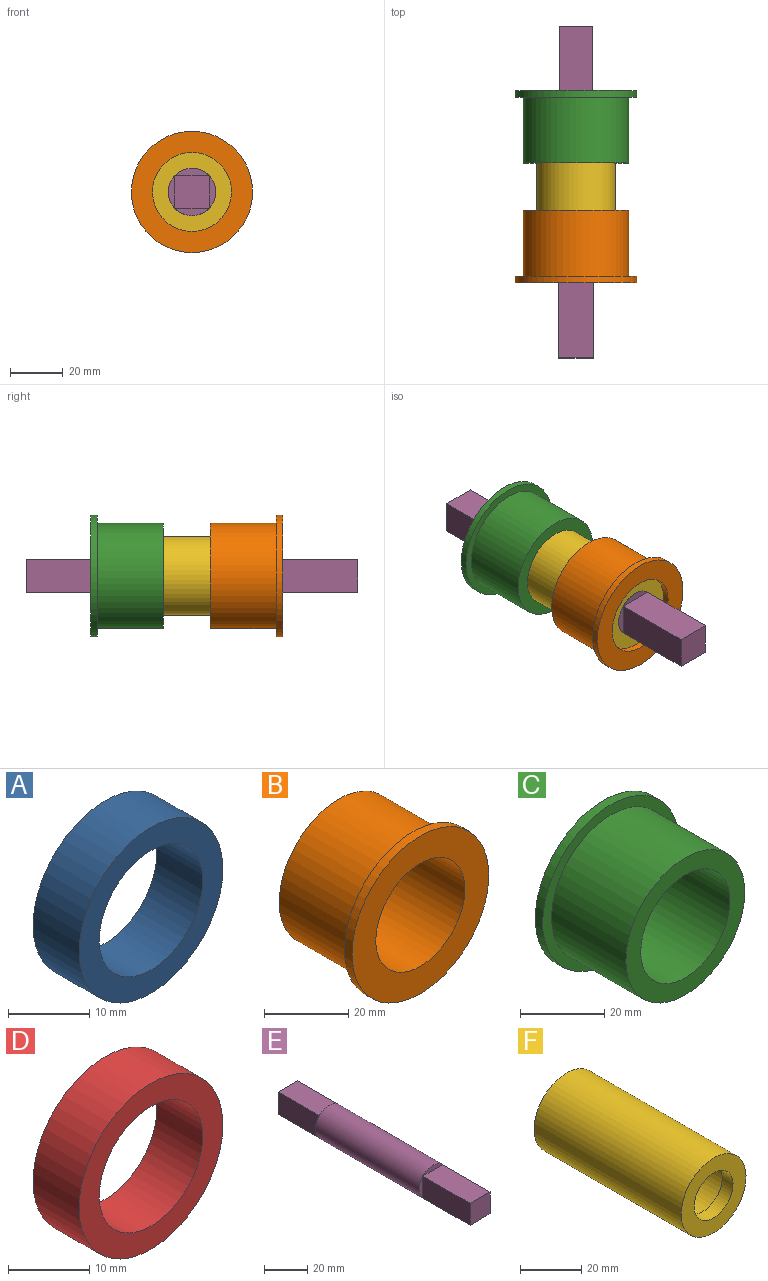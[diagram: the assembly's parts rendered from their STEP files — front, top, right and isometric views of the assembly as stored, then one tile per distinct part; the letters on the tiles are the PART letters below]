
ASSEMBLY  parts=6 mates=10
PART A: 4 faces, bbox 25x8x25 mm
  f0: cylinder r=9mm len=18mm, axis (0,1,0), area 452.4mm2, adj f2,f3
  f1: cylinder r=12.5mm len=25mm, axis (0,1,0), area 628.3mm2, adj f2,f3
  f2: plane 25x25mm, normal (0,-1,0), area 236.4mm2, adj f0,f1
  f3: plane 25x25mm, normal (0,1,0), area 236.4mm2, adj f0,f1
PART B: 6 faces, bbox 46x27.5x46 mm
  f0: cylinder r=15mm len=30mm, axis (0,1,0), area 2591.8mm2, adj f2,f5
  f1: cylinder r=23mm len=46mm, axis (0,1,0), area 361.3mm2, adj f2,f3
  f2: plane 46x46mm, normal (0,-1,0), area 955mm2, adj f0,f1
  f3: plane 46x46mm, normal (0,1,0), area 405.3mm2, adj f1,f4
  f4: cylinder r=20mm len=40mm, axis (0,-1,0), area 3141.6mm2, adj f3,f5
  f5: plane 40x40mm, normal (0,1,0), area 549.8mm2, adj f0,f4
PART C: 6 faces, bbox 46x27.5x46 mm
  f0: cylinder r=15mm len=30mm, axis (0,-1,0), area 2591.8mm2, adj f2,f5
  f1: cylinder r=23mm len=46mm, axis (0,-1,0), area 361.3mm2, adj f2,f3
  f2: plane 46x46mm, normal (0,1,0), area 955mm2, adj f0,f1
  f3: plane 46x46mm, normal (0,-1,0), area 405.3mm2, adj f1,f4
  f4: cylinder r=20mm len=40mm, axis (0,1,0), area 3141.6mm2, adj f3,f5
  f5: plane 40x40mm, normal (0,-1,0), area 549.8mm2, adj f0,f4
PART D: 4 faces, bbox 25x8x25 mm
  f0: cylinder r=9mm len=18mm, axis (0,-1,0), area 452.4mm2, adj f2,f3
  f1: cylinder r=12.5mm len=25mm, axis (0,-1,0), area 628.3mm2, adj f2,f3
  f2: plane 25x25mm, normal (0,1,0), area 236.4mm2, adj f0,f1
  f3: plane 25x25mm, normal (0,-1,0), area 236.4mm2, adj f0,f1
PART E: 19 faces, bbox 18x126x18 mm
  f0: plane 12.67x2.61mm, normal (0,1,0), area 22.7mm2, adj f6,f14
  f1: plane 12.67x2.61mm, normal (0,1,0), area 22.7mm2, adj f6,f16
  f2: plane 12.79x2.67mm, normal (0,1,0), area 23.5mm2, adj f6,f15
  f3: plane 12.4x2.48mm, normal (0,-1,0), area 21.1mm2, adj f6,f9
  f4: plane 13.05x2.8mm, normal (0,-1,0), area 25.2mm2, adj f6,f12
  f5: plane 12.4x2.48mm, normal (0,-1,0), area 21.1mm2, adj f6,f11
  f6: cylinder r=9mm len=68mm, axis (0,1,0), area 3845.3mm2, adj f0,f1,f2,f3,f4,f5,f7,f8
  f7: plane 13.05x2.8mm, normal (0,-1,0), area 25.2mm2, adj f6,f10
  f8: plane 12.79x2.67mm, normal (0,1,0), area 23.5mm2, adj f6,f17
  f9: plane 31x12.4mm, normal (-1,0,0), area 384.3mm2, adj f3,f10,f12,f13
  f10: plane 31x13.05mm, normal (0,0,-1), area 404.5mm2, adj f7,f9,f11,f13
  f11: plane 31x12.4mm, normal (1,0,0), area 384.3mm2, adj f5,f10,f12,f13
  f12: plane 31x13.05mm, normal (0,0,1), area 404.5mm2, adj f4,f9,f11,f13
  f13: plane 13.05x12.4mm, normal (0,-1,0), area 161.8mm2, adj f9,f10,f11,f12
  f14: plane 27x12.67mm, normal (1,0,0), area 342.1mm2, adj f0,f15,f17,f18
  f15: plane 27x12.79mm, normal (0,0,-1), area 345.2mm2, adj f2,f14,f16,f18
  f16: plane 27x12.67mm, normal (-1,0,0), area 342.1mm2, adj f1,f15,f17,f18
  f17: plane 27x12.79mm, normal (0,0,1), area 345.2mm2, adj f8,f14,f16,f18
  f18: plane 12.79x12.67mm, normal (0,1,0), area 162mm2, adj f14,f15,f16,f17
PART F: 8 faces, bbox 30x68x30 mm
  f0: plane 25x25mm, normal (0,1,0), area 236.4mm2, adj f1,f4
  f1: cylinder r=9mm len=18mm, axis (0,-1,0), area 282.7mm2, adj f0,f3
  f2: cylinder r=15mm len=68mm, axis (0,-1,0), area 6408.8mm2, adj f3,f7
  f3: plane 30x30mm, normal (0,-1,0), area 452.4mm2, adj f1,f2
  f4: cylinder r=12.5mm len=58mm, axis (0,-1,0), area 4555.3mm2, adj f0,f5
  f5: plane 25x25mm, normal (0,-1,0), area 236.4mm2, adj f4,f6
  f6: cylinder r=9mm len=18mm, axis (0,1,0), area 282.7mm2, adj f5,f7
  f7: plane 30x30mm, normal (0,1,0), area 452.4mm2, adj f2,f6
PLACE A t=(-57.63,34.28,-68.8)mm
PLACE B t=(-57.63,34.28,-68.8)mm
PLACE C t=(-57.63,34.28,-68.8)mm
PLACE D t=(-57.63,34.28,-68.8)mm
PLACE E t=(-57.63,34.28,-68.8)mm
PLACE F t=(-57.63,34.28,-68.8)mm
MATE cylindrical F.f4 <-> E.f6  axis (0,-1,0) through (-57.63,0.28,-68.8)mm
MATE cylindrical E.f6 <-> D.f0  axis (0,1,0) through (-57.63,0.28,-68.8)mm
MATE planar D.f1 <-> F.f4  axis (0,-1,0) through (-57.63,-28.72,-68.8)mm
MATE planar F.f4 <-> C.f1  axis (0,1,0) through (-57.63,34.28,-68.8)mm
MATE planar E.f1 <-> A.f1  axis (0,1,0) through (-65.08,34.28,-68.8)mm
MATE cylindrical F.f2 <-> B.f4  axis (0,-1,0) through (-57.63,0.28,-68.8)mm
MATE cylindrical E.f6 <-> A.f0  axis (0,1,0) through (-57.63,0.28,-68.8)mm
MATE planar F.f4 <-> B.f1  axis (0,-1,0) through (-57.63,-33.72,-68.8)mm
MATE cylindrical C.f4 <-> F.f2  axis (0,1,0) through (-57.63,21.78,-68.8)mm
MATE planar E.f3 <-> D.f1  axis (0,-1,0) through (-65.16,-33.72,-68.8)mm
